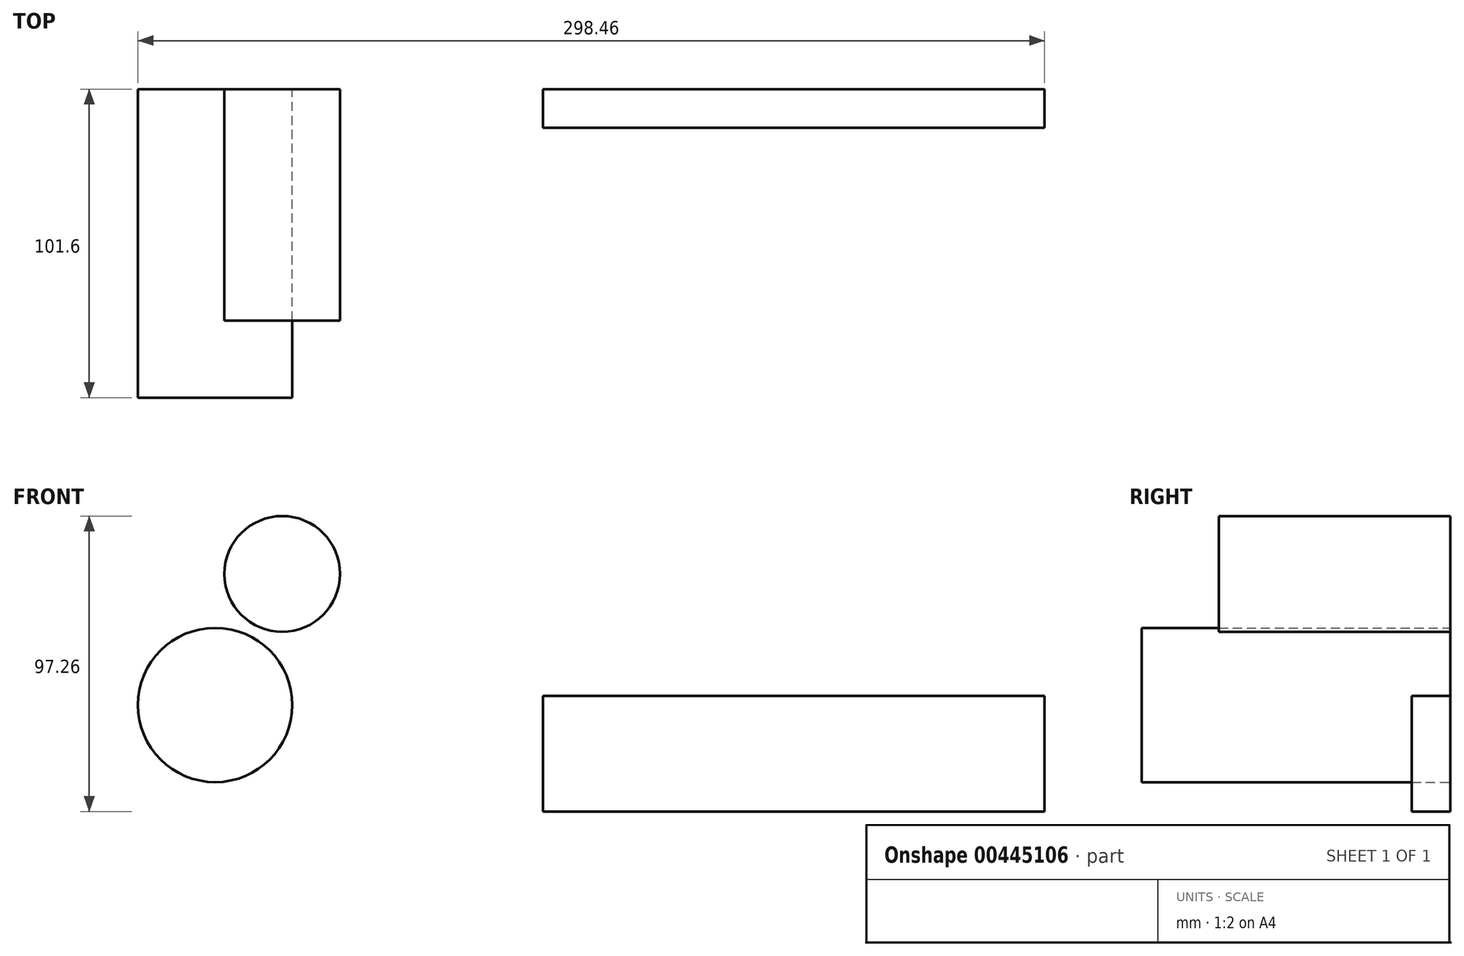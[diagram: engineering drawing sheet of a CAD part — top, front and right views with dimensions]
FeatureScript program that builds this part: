
annotation { "Feature Type Name" : "Feature", "Feature Type Description" : "" }
export const myFeature = defineFeature(function(context is Context, id is Id, definition is map)
    precondition{}
    {
        {
            var Q0;
            Q0=qCreatedBy(makeId("Front.planeOp"),FACE);
            var sketch = newSketch(context, id + "F0", { "sketchPlane" : qUnion([Q0])});
            skCircle(sketch, "E0", {"center": v(-40.7, 37.28) * mm, "radius": 19.05 * mm});
            skCircle(sketch, "E1", {"center": v(-62.79, -5.88) * mm, "radius": 25.4 * mm});
            skLineSegment(sketch, "E2.bottom", {"start": v(45.17, -2.83) * mm, "end": v(210.27, -2.83) * mm});
            skLineSegment(sketch, "E2.top", {"start": v(45.17, -40.93) * mm, "end": v(210.27, -40.93) * mm});
            skLineSegment(sketch, "E2.left", {"start": v(45.17, -2.83) * mm, "end": v(45.17, -40.93) * mm});
            skLineSegment(sketch, "E2.right", {"start": v(210.27, -2.83) * mm, "end": v(210.27, -40.93) * mm});
            skSolve(sketch);
        }
        {
            var Q0;
            Q0=makeQuery(id+"F0.imprint","IMPRINT",FACE,{"disambiguationData":[TD([[makeQuery(id+"F0.imprint","IMPRINT",EDGE,{"derivedFrom":sQuery(id+"F0.wireOp",EDGE,"E0")}),1.0]])]});
            extrude(context, id + "F1", {"entities" : qUnion([Q0]), "depth" : 76.2 * mm});
        }
        {
            var Q0;
            Q0=makeQuery(id+"F0.imprint","IMPRINT",FACE,{"disambiguationData":[TD([[makeQuery(id+"F0.imprint","IMPRINT",EDGE,{"derivedFrom":sQuery(id+"F0.wireOp",EDGE,"E1")}),1.0]])]});
            extrude(context, id + "F2", {"entities" : qUnion([Q0]), "depth" : 101.6 * mm});
        }
        {
            var Q0;
            Q0=makeQuery(id+"F0.imprint","IMPRINT",FACE,{"disambiguationData":[TD([[makeQuery(id+"F0.imprint","IMPRINT",EDGE,{"derivedFrom":sQuery(id+"F0.wireOp",EDGE,"E2.bottom")}),-1.0]])]});
            extrude(context, id + "F3", {"entities" : qUnion([Q0]), "depth" : 12.7 * mm});
        }
    });
